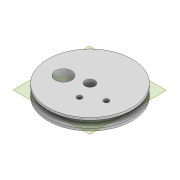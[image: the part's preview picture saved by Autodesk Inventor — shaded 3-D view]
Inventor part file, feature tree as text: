
AUTODESK INVENTOR PART (.ipt)
format: ipt  version: 2022 (Build 260153000, 153)  size: 274,432 bytes
history: native  units: mm
features: extrude x7, sketch x6, plane x3, pattern_circular x1, fillet x1, mirror x1, projected_geometry x1
ambient origin geometry x8: Origin, YZ Plane, XZ Plane, XY Plane, X Axis, Y Axis, Z Axis, Center Point
bodies: Solid1 (feature_tree)
feature tree (20):
  extrude  "Extrusion1"  Depth=30.0mm
  extrude  "Extrusion2"  Depth=3.0mm TaperAngle=0.0deg
  pattern_circular  "Circular Pattern1"  Count=5 Angle=360.0deg
  plane  "Work Plane1"
  plane  "Work Plane2"
  extrude  "Extrusion3"  [1 undecoded]
  extrude  "Extrusion4"  Depth=3.0mm
  fillet  "Fillet1"  Radius=1.5mm
  plane  "Work Plane3"
  extrude  "Extrusion5"  Depth=3.0mm
  mirror  "Mirror1"
  sketch  "Sketch6"  dims[d13=9.599311mm d14=-9.599311mm d15=1.5mm d16=1.5mm d17=1.7mm d18=10.0mm d19=0.0mm d20=1.5mm d21=1.5mm d22=1.7mm d23=10.0mm d24=0.0mm d25=1.0mm d26=36.0mm d27=1.0mm d28=0.0mm d29=2.1mm d30=10.0mm d31=3.0mm d32=2.1mm d33=7.5mm d35=5.0mm d36=0.0mm d37=100.0mm d38=0.0mm d39=3.0mm]
  extrude  "Extrusion6"  Depth=10.0mm TaperAngle=0.0deg
  extrude  "Extrusion7"  Depth=3.0mm
  sketch  "Sketch1"  dims[d0=4.2mm d2=30.0mm]
  sketch  "Sketch2"  dims[d3=4.0mm d4=3.0mm d5=0.0mm]
  sketch  "Sketch3"  dims[d6=7.0mm]
  sketch  "Sketch4"  dims[d7=9.0mm]
  sketch  "Sketch5"  dims[d8=10.0mm d9=0.0mm d10=50.0mm d11=360.0deg]
  projected_geometry  "Projected Loop1"
note: 1 required parameter value undecoded (feature->parameter linkage not recoverable at this tier; creation-order binding heuristic only, values carry confidence <= 0.55)
